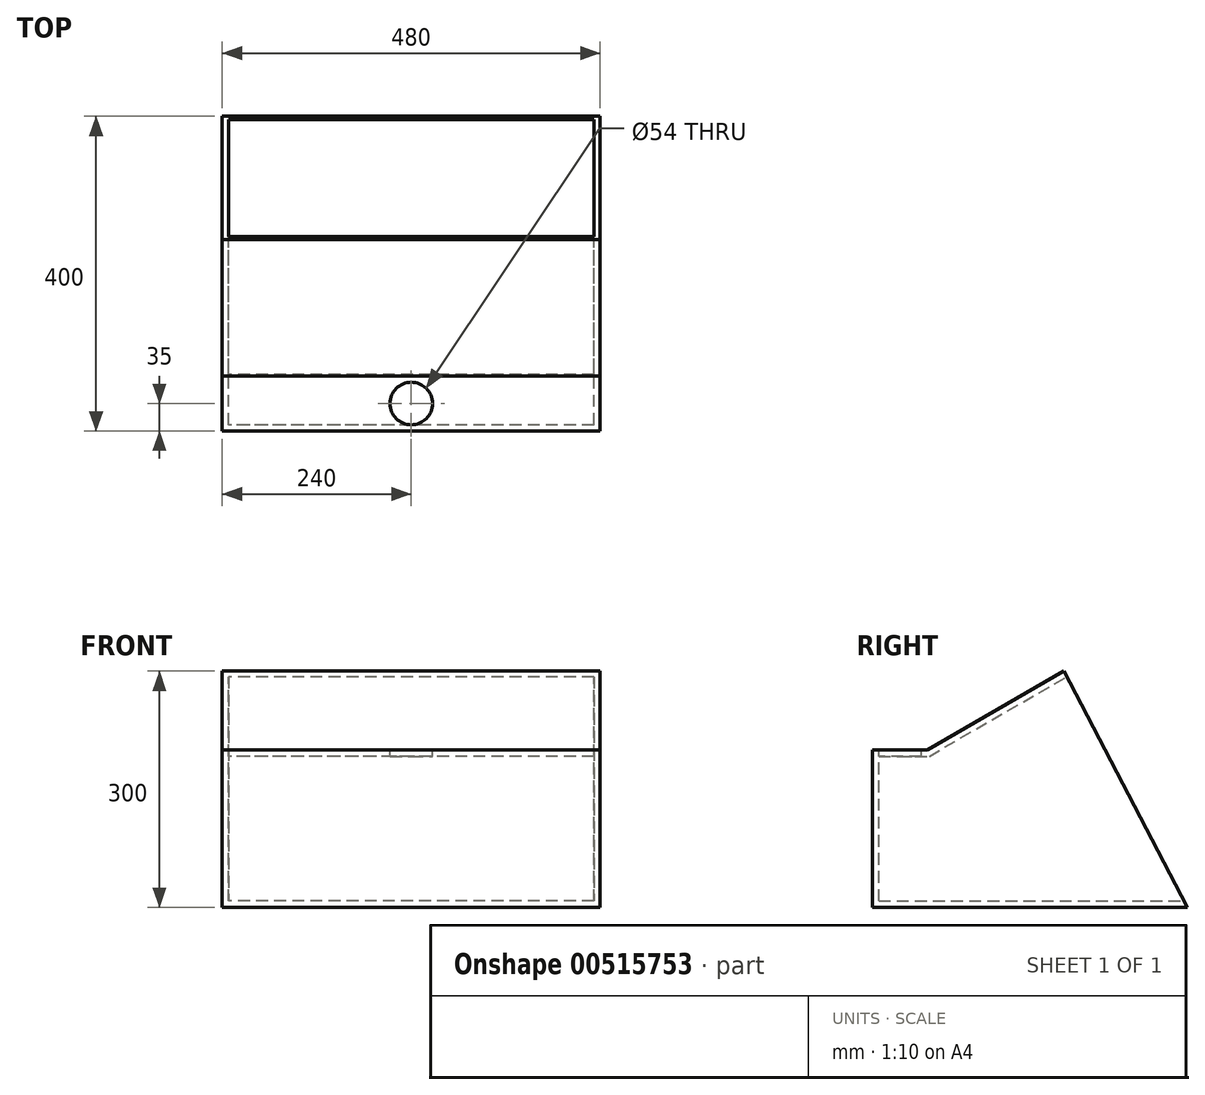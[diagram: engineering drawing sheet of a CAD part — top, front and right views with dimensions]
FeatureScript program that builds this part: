
annotation { "Feature Type Name" : "Feature", "Feature Type Description" : "" }
export const myFeature = defineFeature(function(context is Context, id is Id, definition is map)
    precondition{}
    {
        {
            var Q0;
            Q0=qCreatedBy(makeId("Right.planeOp"),FACE);
            var sketch = newSketch(context, id + "F0", { "sketchPlane" : qUnion([Q0])});
            skLineSegment(sketch, "E0", {"start": v(0, 0) * mm, "end": v(400, 0) * mm});
            skLineSegment(sketch, "E1", {"start": v(0, 0) * mm, "end": v(0, 200) * mm});
            skLineSegment(sketch, "E2", {"start": v(0, 200) * mm, "end": v(70, 200) * mm});
            skLineSegment(sketch, "E3", {"start": v(70, 200) * mm, "end": v(243.2, 300) * mm});
            skLineSegment(sketch, "E4", {"start": v(243.2, 300) * mm, "end": v(400, 0) * mm});
            skSolve(sketch);
        }
        {
            var Q0;
            Q0=makeQuery(id+"F0.imprint","IMPRINT",FACE,{"disambiguationData":[TD([[makeQuery(id+"F0.imprint","IMPRINT",EDGE,{"derivedFrom":sQuery(id+"F0.wireOp",EDGE,"E0")}),1.0]])]});
            extrude(context, id + "F1", {"entities" : qUnion([Q0]), "depth" : 480 * mm, "offsetDistance" : 25 * mm});
        }
        {
            var Q0;
            Q0=makeQuery(id+"F1.opExtrude","SWEPT_FACE",FACE,{"disambiguationData":[OSD([sQuery(id+"F0.wireOp",EDGE,"E4")])]});
            shell(context, id + "F2", {"entities" : qUnion([Q0]), "thickness" : 8 * mm});
        }
        {
            var Q0;
            Q0=makeQuery(id+"F1.opExtrude","SWEPT_FACE",FACE,{"disambiguationData":[OSD([sQuery(id+"F0.wireOp",EDGE,"E2")])]});
            var sketch = newSketch(context, id + "F3", { "sketchPlane" : qUnion([Q0])});
            skLineSegment(sketch, "E5", {"start": v(240, 0) * mm, "end": v(240, 70) * mm, "construction": true});
            skCircle(sketch, "E6", {"center": v(240, 35) * mm, "radius": 27 * mm});
            skSolve(sketch);
        }
        {
            var Q0;
            Q0=makeQuery(id+"F3.imprint","IMPRINT",FACE,{"disambiguationData":[TD([[makeQuery(id+"F3.imprint","IMPRINT",EDGE,{"derivedFrom":sQuery(id+"F3.wireOp",EDGE,"E6")}),1.0]])]});
            extrude(context, id + "F4", {"entities" : qUnion([Q0]), "operationType" : NewBodyOperationType.REMOVE, "oppositeDirection" : true, "depth" : 25 * mm, "offsetDistance" : 25 * mm});
        }
    });
